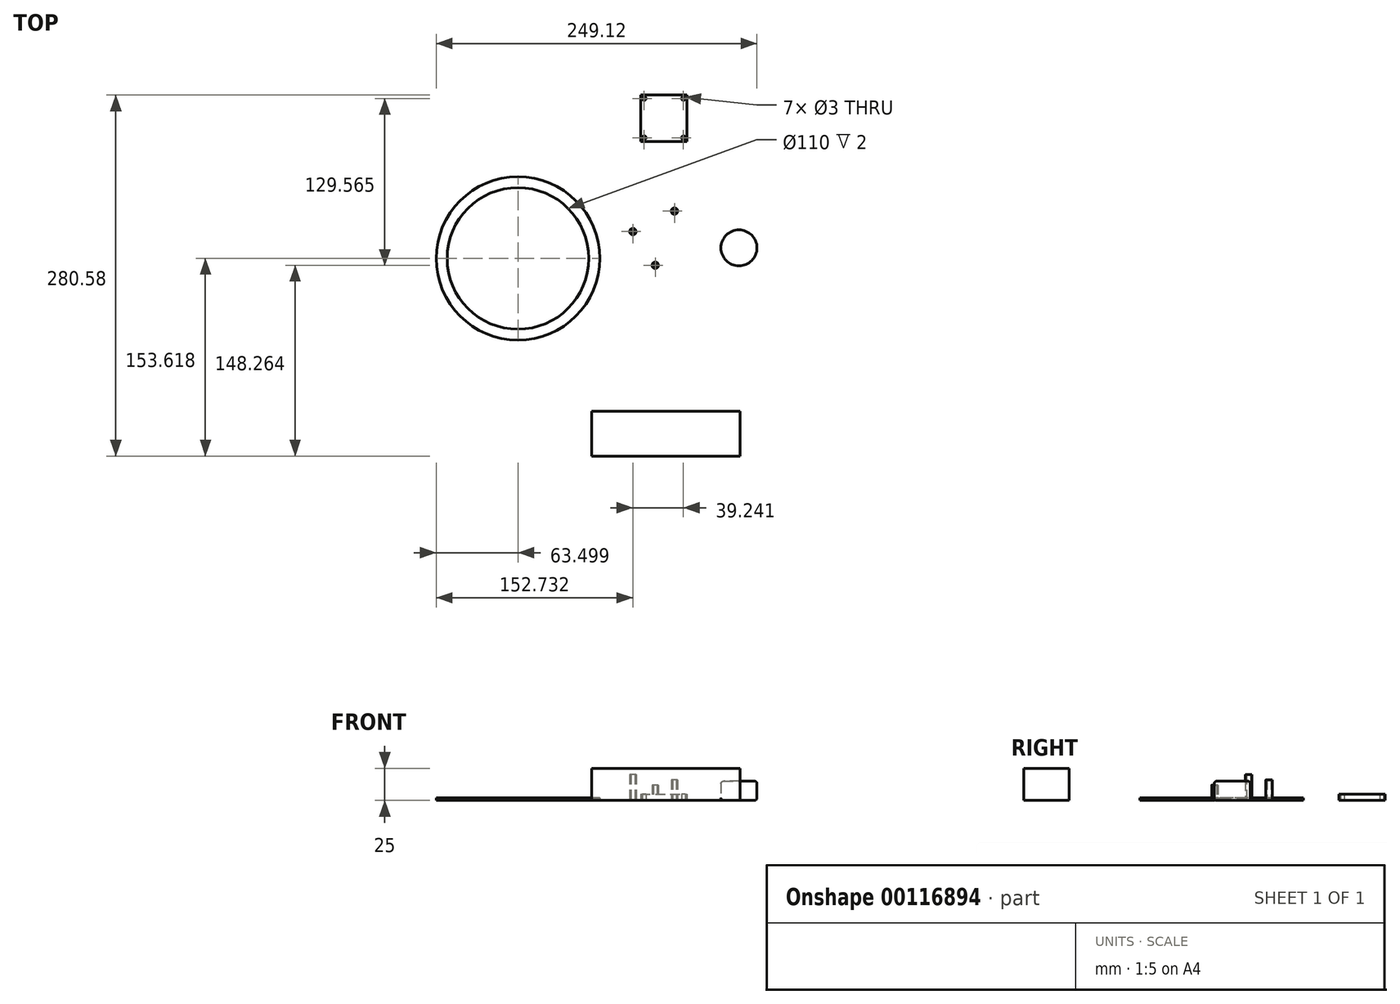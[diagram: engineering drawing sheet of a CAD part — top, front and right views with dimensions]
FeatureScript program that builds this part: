
annotation { "Feature Type Name" : "Feature", "Feature Type Description" : "" }
export const myFeature = defineFeature(function(context is Context, id is Id, definition is map)
    precondition{}
    {
        {
            var Q0;
            Q0=qCreatedBy(makeId("Top.planeOp"),FACE);
            var sketch = newSketch(context, id + "F0", { "sketchPlane" : qUnion([Q0])});
            skCircle(sketch, "E0", {"center": v(-54.15, 35.16) * mm, "radius": 2.5 * mm});
            skCircle(sketch, "E1", {"center": v(-54.15, 35.16) * mm, "radius": 1.5 * mm});
            skSolve(sketch);
        }
        {
            var Q0;
            Q0 = qSketchRegion(id + "F0", true);
            extrude(context, id + "F1", {"entities" : qUnion([Q0]), "depth" : 20 * mm});
        }
        {
            var Q0;
            Q0=qCreatedBy(makeId("Top.planeOp"),FACE);
            var sketch = newSketch(context, id + "F2", { "sketchPlane" : qUnion([Q0])});
            skCircle(sketch, "E2", {"center": v(28.24, 22.47) * mm, "radius": 14 * mm});
            skSolve(sketch);
        }
        {
            var Q0;
            Q0 = qSketchRegion(id + "F2", true);
            extrude(context, id + "F3", {"entities" : qUnion([Q0]), "depth" : 15 * mm});
        }
        {
            var Q0;
            Q0=makeQuery(id+"F3.opExtrude","CAP_EDGE",EDGE,{"disambiguationData":[OSD([sQuery(id+"F2.wireOp",EDGE,"E2")])],"isStart":false});
            var Q1;
            Q1=makeQuery(id+"F3.opExtrude","CAP_EDGE",EDGE,{"disambiguationData":[OSD([sQuery(id+"F2.wireOp",EDGE,"E2")])],"isStart":true});
            fillet(context, id + "F4", {"entities" : qUnion([Q0, Q1]), "radius" : 2 * mm, "tangentPropagation" : true, "allowEdgeOverflow" : false});
        }
        {
            var Q0;
            Q0=qCreatedBy(makeId("Top.planeOp"),FACE);
            var sketch = newSketch(context, id + "F5", { "sketchPlane" : qUnion([Q0])});
            skCircle(sketch, "E3", {"center": v(-143.38, 14.32) * mm, "radius": 63.5 * mm});
            skCircle(sketch, "E4", {"center": v(-143.38, 14.32) * mm, "radius": 55 * mm});
            skSolve(sketch);
        }
        {
            var Q0;
            Q0 = qSketchRegion(id + "F5", true);
            extrude(context, id + "F6", {"entities" : qUnion([Q0]), "depth" : 2 * mm});
        }
        {
            var Q0;
            Q0=qCreatedBy(makeId("Top.planeOp"),FACE);
            var sketch = newSketch(context, id + "F7", { "sketchPlane" : qUnion([Q0])});
            skCircle(sketch, "E5", {"center": v(-21.88, 51.09) * mm, "radius": 2.5 * mm});
            skCircle(sketch, "E6", {"center": v(-21.88, 51.09) * mm, "radius": 1.5 * mm});
            skSolve(sketch);
        }
        {
            var Q0;
            Q0 = qSketchRegion(id + "F7", true);
            extrude(context, id + "F8", {"entities" : qUnion([Q0]), "depth" : 16 * mm});
        }
        {
            var Q0;
            Q0=qCreatedBy(makeId("Top.planeOp"),FACE);
            var sketch = newSketch(context, id + "F9", { "sketchPlane" : qUnion([Q0])});
            skLineSegment(sketch, "E7.bottom", {"start": v(-86.07, -104.3) * mm, "end": v(28.93, -104.3) * mm});
            skLineSegment(sketch, "E7.top", {"start": v(-86.07, -139.3) * mm, "end": v(28.93, -139.3) * mm});
            skLineSegment(sketch, "E7.left", {"start": v(-86.07, -104.3) * mm, "end": v(-86.07, -139.3) * mm});
            skLineSegment(sketch, "E7.right", {"start": v(28.93, -104.3) * mm, "end": v(28.93, -139.3) * mm});
            skSolve(sketch);
        }
        {
            var Q0;
            Q0 = qSketchRegion(id + "F9", true);
            extrude(context, id + "F10", {"entities" : qUnion([Q0]), "depth" : 25 * mm});
        }
        {
            var Q0;
            Q0=qCreatedBy(makeId("Top.planeOp"),FACE);
            var sketch = newSketch(context, id + "F11", { "sketchPlane" : qUnion([Q0])});
            skCircle(sketch, "E8", {"center": v(-36.78, 8.96) * mm, "radius": 2.5 * mm});
            skCircle(sketch, "E9", {"center": v(-36.78, 8.96) * mm, "radius": 1.5 * mm});
            skSolve(sketch);
        }
        {
            var Q0;
            Q0 = qSketchRegion(id + "F11", true);
            extrude(context, id + "F12", {"entities" : qUnion([Q0]), "depth" : 12 * mm});
        }
        {
            var Q0;
            Q0=qCreatedBy(makeId("Top.planeOp"),FACE);
            var sketch = newSketch(context, id + "F13", { "sketchPlane" : qUnion([Q0])});
            skLineSegment(sketch, "E10.bottom", {"start": v(-48.16, 141.28) * mm, "end": v(-12.16, 141.28) * mm});
            skLineSegment(sketch, "E10.top", {"start": v(-48.16, 105.28) * mm, "end": v(-12.16, 105.28) * mm});
            skLineSegment(sketch, "E10.left", {"start": v(-48.16, 141.28) * mm, "end": v(-48.16, 105.28) * mm});
            skLineSegment(sketch, "E10.right", {"start": v(-12.16, 141.28) * mm, "end": v(-12.16, 105.28) * mm});
            skCircle(sketch, "E11", {"center": v(-45.4, 138.53) * mm, "radius": 1.5 * mm});
            skCircle(sketch, "E12", {"center": v(-14.9, 138.53) * mm, "radius": 1.5 * mm});
            skCircle(sketch, "E13", {"center": v(-45.4, 108.03) * mm, "radius": 1.5 * mm});
            skCircle(sketch, "E14", {"center": v(-14.9, 108.03) * mm, "radius": 1.5 * mm});
            skSolve(sketch);
        }
        {
            var Q0;
            Q0 = qSketchRegion(id + "F13", true);
            extrude(context, id + "F14", {"entities" : qUnion([Q0]), "depth" : 5 * mm});
        }
    });
